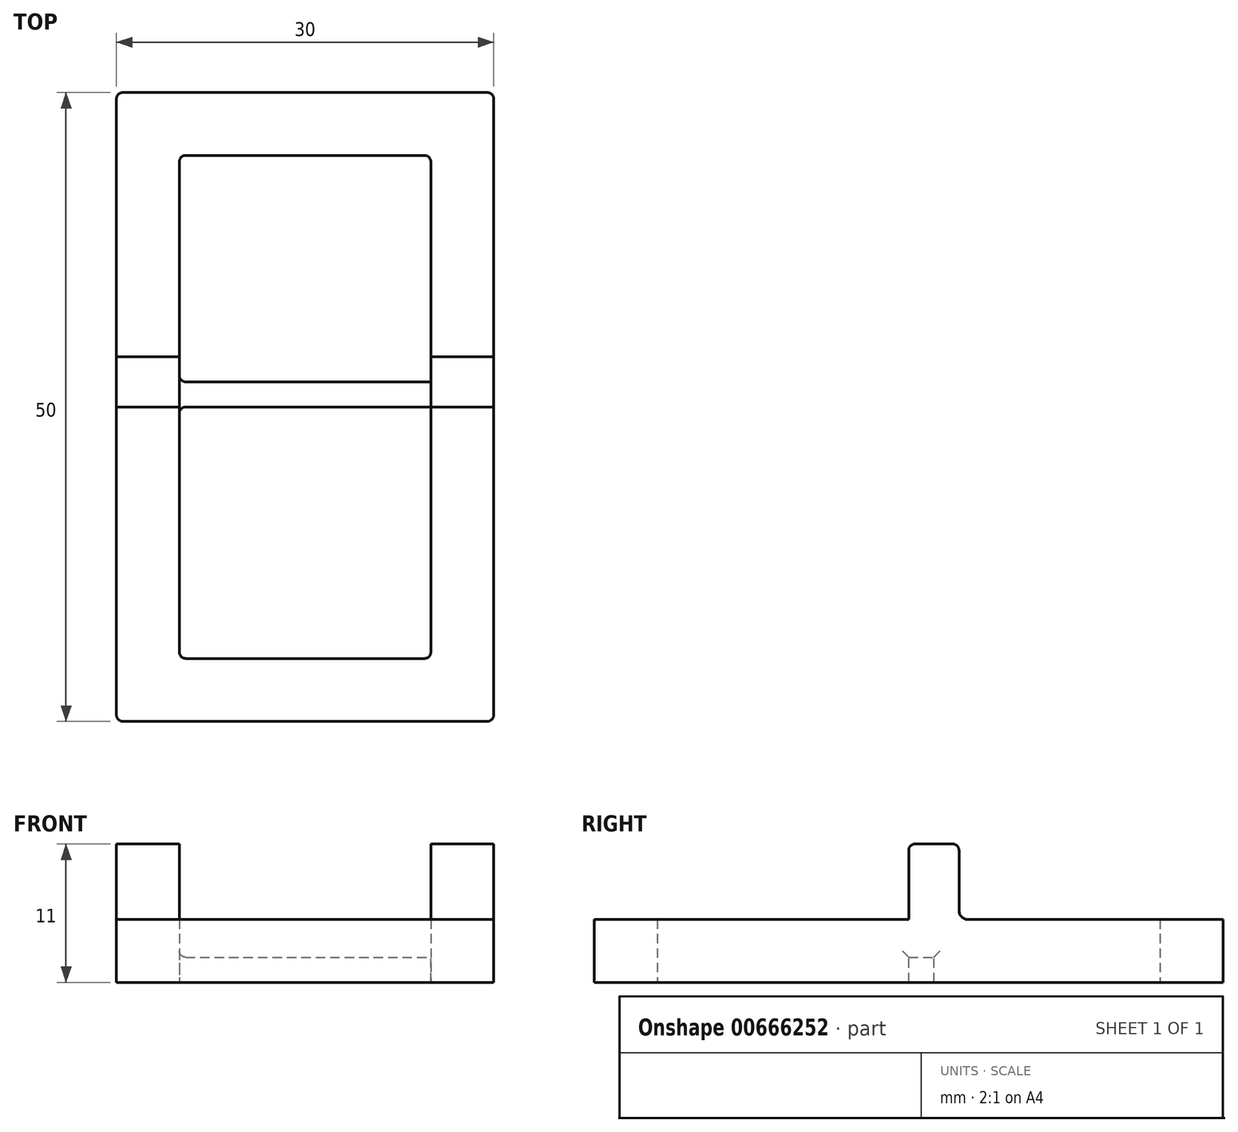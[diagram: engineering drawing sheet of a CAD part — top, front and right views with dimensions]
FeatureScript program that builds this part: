
annotation { "Feature Type Name" : "Feature", "Feature Type Description" : "" }
export const myFeature = defineFeature(function(context is Context, id is Id, definition is map)
    precondition{}
    {
        {
            var Q0;
            Q0=qCreatedBy(makeId("Top.planeOp"),FACE);
            var sketch = newSketch(context, id + "F0", { "sketchPlane" : qUnion([Q0])});
            skLineSegment(sketch, "E0.bottom", {"start": v(0, 0) * mm, "end": v(30, 0) * mm});
            skLineSegment(sketch, "E0.top", {"start": v(0, 50) * mm, "end": v(30, 50) * mm});
            skLineSegment(sketch, "E0.left", {"start": v(0, 0) * mm, "end": v(0, 50) * mm});
            skLineSegment(sketch, "E0.right", {"start": v(30, 0) * mm, "end": v(30, 50) * mm});
            skLineSegment(sketch, "E1.0", {"start": v(5, 5) * mm, "end": v(5, 45) * mm});
            skLineSegment(sketch, "E1.1", {"start": v(5, 5) * mm, "end": v(25, 5) * mm});
            skLineSegment(sketch, "E1.2", {"start": v(25, 5) * mm, "end": v(25, 45) * mm});
            skLineSegment(sketch, "E1.3", {"start": v(5, 45) * mm, "end": v(25, 45) * mm});
            skSolve(sketch);
        }
        {
            var Q0;
            Q0 = qSketchRegion(id + "F0", true);
            extrude(context, id + "F1", {"entities" : qUnion([Q0]), "depth" : 5 * mm, "offsetDistance" : 25 * mm});
        }
        {
            var Q0;
            Q0=makeQuery(id+"F1.opExtrude","CAP_FACE",FACE,{"disambiguationData":[OSD([sQuery(id+"F0.wireOp",EDGE,"E0.bottom"),sQuery(id+"F0.wireOp",EDGE,"E0.top"),sQuery(id+"F0.wireOp",EDGE,"E0.left"),sQuery(id+"F0.wireOp",EDGE,"E0.right"),sQuery(id+"F0.wireOp",EDGE,"E1.0"),sQuery(id+"F0.wireOp",EDGE,"E1.1"),sQuery(id+"F0.wireOp",EDGE,"E1.2"),sQuery(id+"F0.wireOp",EDGE,"E1.3")])],"isStart":false});
            var sketch = newSketch(context, id + "F2", { "sketchPlane" : qUnion([Q0])});
            skLineSegment(sketch, "E2.bottom", {"start": v(5, 25) * mm, "end": v(0, 25) * mm});
            skLineSegment(sketch, "E2.top", {"start": v(5, 29) * mm, "end": v(0, 29) * mm});
            skLineSegment(sketch, "E2.left", {"start": v(5, 25) * mm, "end": v(5, 29) * mm});
            skLineSegment(sketch, "E2.right", {"start": v(0, 25) * mm, "end": v(0, 29) * mm});
            skLineSegment(sketch, "E3", {"start": v(5, 25) * mm, "end": v(25, 25) * mm, "construction": true});
            skLineSegment(sketch, "E4.bottom", {"start": v(25, 25) * mm, "end": v(30, 25) * mm});
            skLineSegment(sketch, "E4.top", {"start": v(25, 29) * mm, "end": v(30, 29) * mm});
            skLineSegment(sketch, "E4.left", {"start": v(25, 25) * mm, "end": v(25, 29) * mm});
            skLineSegment(sketch, "E4.right", {"start": v(30, 25) * mm, "end": v(30, 29) * mm});
            skSolve(sketch);
        }
        {
            var Q0;
            Q0=makeQuery(id+"F2.imprint","IMPRINT",FACE,{"disambiguationData":[TD([[makeQuery(id+"F2.imprint","IMPRINT",EDGE,{"derivedFrom":sQuery(id+"F2.wireOp",EDGE,"E2.bottom")}),-1.0]])]});
            var Q1;
            Q1=makeQuery(id+"F2.imprint","IMPRINT",FACE,{"disambiguationData":[TD([[makeQuery(id+"F2.imprint","IMPRINT",EDGE,{"derivedFrom":sQuery(id+"F2.wireOp",EDGE,"E4.bottom")}),1.0]])]});
            extrude(context, id + "F3", {"entities" : qUnion([Q0, Q1]), "operationType" : NewBodyOperationType.ADD, "depth" : 6 * mm, "offsetDistance" : 25 * mm});
        }
        {
            var Q0;
            Q0=makeQuery(id+"F3.boolean.opBoolean","MERGE",FACE,{"derivedFrom":[makeQuery(id+"F1.opExtrude","SWEPT_FACE",FACE,{"disambiguationData":[OSD([sQuery(id+"F0.wireOp",EDGE,"E1.2")])]}),makeQuery(id+"F3.opExtrude","SWEPT_FACE",FACE,{"disambiguationData":[OSD([sQuery(id+"F2.wireOp",EDGE,"E4.left")])]})]});
            var sketch = newSketch(context, id + "F4", { "sketchPlane" : qUnion([Q0])});
            skLineSegment(sketch, "E5.bottom", {"start": v(-25, 0) * mm, "end": v(-27, 0) * mm});
            skLineSegment(sketch, "E5.top", {"start": v(-25, 2) * mm, "end": v(-27, 2) * mm});
            skLineSegment(sketch, "E5.left", {"start": v(-25, 0) * mm, "end": v(-25, 2) * mm});
            skLineSegment(sketch, "E5.right", {"start": v(-27, 0) * mm, "end": v(-27, 2) * mm});
            skSolve(sketch);
        }
        {
            var Q0;
            Q0 = qSketchRegion(id + "F4", true);
            extrude(context, id + "F5", {"entities" : qUnion([Q0]), "operationType" : NewBodyOperationType.ADD, "depth" : 20.1 * mm, "offsetDistance" : 25 * mm});
        }
        {
            var Q0;
            Q0=makeQuery(id+"F3.opExtrude","CAP_EDGE",EDGE,{"disambiguationData":[OSD([sQuery(id+"F2.wireOp",EDGE,"E4.top")])],"isStart":false});
            var Q1;
            Q1=makeQuery(id+"F3.opExtrude","CAP_EDGE",EDGE,{"disambiguationData":[OSD([sQuery(id+"F2.wireOp",EDGE,"E4.bottom")])],"isStart":false});
            var Q2;
            Q2=makeQuery(id+"F3.opExtrude","CAP_EDGE",EDGE,{"disambiguationData":[OSD([sQuery(id+"F2.wireOp",EDGE,"E2.bottom")])],"isStart":false});
            var Q3;
            Q3=makeQuery(id+"F3.opExtrude","CAP_EDGE",EDGE,{"disambiguationData":[OSD([sQuery(id+"F2.wireOp",EDGE,"E2.top")])],"isStart":false});
            var Q4;
            Q4=makeQuery(id+"F1.opExtrude","SWEPT_EDGE",EDGE,{"disambiguationData":[OSD([sQuery(id+"F0.wireOp",EDGE,"E0.bottom"),sQuery(id+"F0.wireOp",EDGE,"E0.right")])]});
            var Q5;
            Q5=makeQuery(id+"F1.opExtrude","SWEPT_EDGE",EDGE,{"disambiguationData":[OSD([sQuery(id+"F0.wireOp",EDGE,"E1.1"),sQuery(id+"F0.wireOp",EDGE,"E1.2")])]});
            var Q6;
            Q6=makeQuery(id+"F1.opExtrude","SWEPT_EDGE",EDGE,{"disambiguationData":[OSD([sQuery(id+"F0.wireOp",EDGE,"E0.top"),sQuery(id+"F0.wireOp",EDGE,"E0.right")])]});
            var Q7;
            Q7=makeQuery(id+"F1.opExtrude","SWEPT_EDGE",EDGE,{"disambiguationData":[OSD([sQuery(id+"F0.wireOp",EDGE,"E0.top"),sQuery(id+"F0.wireOp",EDGE,"E0.left")])]});
            var Q8;
            Q8=makeQuery(id+"F1.opExtrude","SWEPT_EDGE",EDGE,{"disambiguationData":[OSD([sQuery(id+"F0.wireOp",EDGE,"E1.0"),sQuery(id+"F0.wireOp",EDGE,"E1.3")])]});
            var Q9;
            Q9=makeQuery(id+"F1.opExtrude","SWEPT_EDGE",EDGE,{"disambiguationData":[OSD([sQuery(id+"F0.wireOp",EDGE,"E1.0"),sQuery(id+"F0.wireOp",EDGE,"E1.1")])]});
            var Q10;
            Q10=makeQuery(id+"F5.boolean.opBoolean","INTERSECT",EDGE,{"derivedFrom":[makeQuery(id+"F3.boolean.opBoolean","MERGE",FACE,{"derivedFrom":[makeQuery(id+"F1.opExtrude","SWEPT_FACE",FACE,{"disambiguationData":[OSD([sQuery(id+"F0.wireOp",EDGE,"E1.0")])]}),makeQuery(id+"F3.opExtrude","SWEPT_FACE",FACE,{"disambiguationData":[OSD([sQuery(id+"F2.wireOp",EDGE,"E2.left")])]})]}),makeQuery(id+"F5.opExtrude","SWEPT_FACE",FACE,{"disambiguationData":[OSD([sQuery(id+"F4.wireOp",EDGE,"E5.right")])]})]});
            var Q11;
            Q11=makeQuery(id+"F5.boolean.opBoolean","INTERSECT",EDGE,{"derivedFrom":[makeQuery(id+"F3.boolean.opBoolean","MERGE",FACE,{"derivedFrom":[makeQuery(id+"F1.opExtrude","SWEPT_FACE",FACE,{"disambiguationData":[OSD([sQuery(id+"F0.wireOp",EDGE,"E1.0")])]}),makeQuery(id+"F3.opExtrude","SWEPT_FACE",FACE,{"disambiguationData":[OSD([sQuery(id+"F2.wireOp",EDGE,"E2.left")])]})]}),makeQuery(id+"F5.opExtrude","SWEPT_FACE",FACE,{"disambiguationData":[OSD([sQuery(id+"F4.wireOp",EDGE,"E5.top")])]})]});
            var Q12;
            Q12=makeQuery(id+"F5.boolean.opBoolean","INTERSECT",EDGE,{"derivedFrom":[makeQuery(id+"F3.boolean.opBoolean","MERGE",FACE,{"derivedFrom":[makeQuery(id+"F1.opExtrude","SWEPT_FACE",FACE,{"disambiguationData":[OSD([sQuery(id+"F0.wireOp",EDGE,"E1.0")])]}),makeQuery(id+"F3.opExtrude","SWEPT_FACE",FACE,{"disambiguationData":[OSD([sQuery(id+"F2.wireOp",EDGE,"E2.left")])]})]}),makeQuery(id+"F5.opExtrude","SWEPT_FACE",FACE,{"disambiguationData":[OSD([sQuery(id+"F4.wireOp",EDGE,"E5.left")])]})]});
            var Q13;
            Q13=makeQuery(id+"F5.opExtrude","CAP_EDGE",EDGE,{"disambiguationData":[OSD([sQuery(id+"F4.wireOp",EDGE,"E5.left")])],"isStart":true});
            var Q14;
            Q14=makeQuery(id+"F5.opExtrude","CAP_EDGE",EDGE,{"disambiguationData":[OSD([sQuery(id+"F4.wireOp",EDGE,"E5.top")])],"isStart":true});
            var Q15;
            Q15=makeQuery(id+"F1.opExtrude","SWEPT_EDGE",EDGE,{"disambiguationData":[OSD([sQuery(id+"F0.wireOp",EDGE,"E1.2"),sQuery(id+"F0.wireOp",EDGE,"E1.3")])]});
            var Q16;
            Q16=makeQuery(id+"F5.opExtrude","CAP_EDGE",EDGE,{"disambiguationData":[OSD([sQuery(id+"F4.wireOp",EDGE,"E5.right")])],"isStart":true});
            var Q17;
            Q17=makeQuery(id+"F1.opExtrude","SWEPT_EDGE",EDGE,{"disambiguationData":[OSD([sQuery(id+"F0.wireOp",EDGE,"E0.bottom"),sQuery(id+"F0.wireOp",EDGE,"E0.left")])]});
            fillet(context, id + "F6", {"entities" : qUnion([Q0, Q1, Q2, Q3, Q4, Q5, Q6, Q7, Q8, Q9, Q10, Q11, Q12, Q13, Q14, Q15, Q16, Q17]), "radius" : 0.5 * mm, "tangentPropagation" : true, "allowEdgeOverflow" : false});
        }
        {
            var Q0;
            Q0=makeQuery(id+"F3.opExtrude","CAP_EDGE",EDGE,{"disambiguationData":[OSD([sQuery(id+"F2.wireOp",EDGE,"E2.bottom")])],"isStart":true});
            var Q1;
            Q1=makeQuery(id+"F3.opExtrude","CAP_EDGE",EDGE,{"disambiguationData":[OSD([sQuery(id+"F2.wireOp",EDGE,"E4.bottom")])],"isStart":true});
            var Q2;
            Q2=makeQuery(id+"F3.opExtrude","CAP_EDGE",EDGE,{"disambiguationData":[OSD([sQuery(id+"F2.wireOp",EDGE,"E4.top")])],"isStart":true});
            var Q3;
            Q3=makeQuery(id+"F3.opExtrude","CAP_EDGE",EDGE,{"disambiguationData":[OSD([sQuery(id+"F2.wireOp",EDGE,"E2.top")])],"isStart":true});
            fillet(context, id + "F7", {"entities" : qUnion([Q0, Q1, Q2, Q3]), "radius" : 0.7 * mm, "tangentPropagation" : true, "allowEdgeOverflow" : false});
        }
    });
